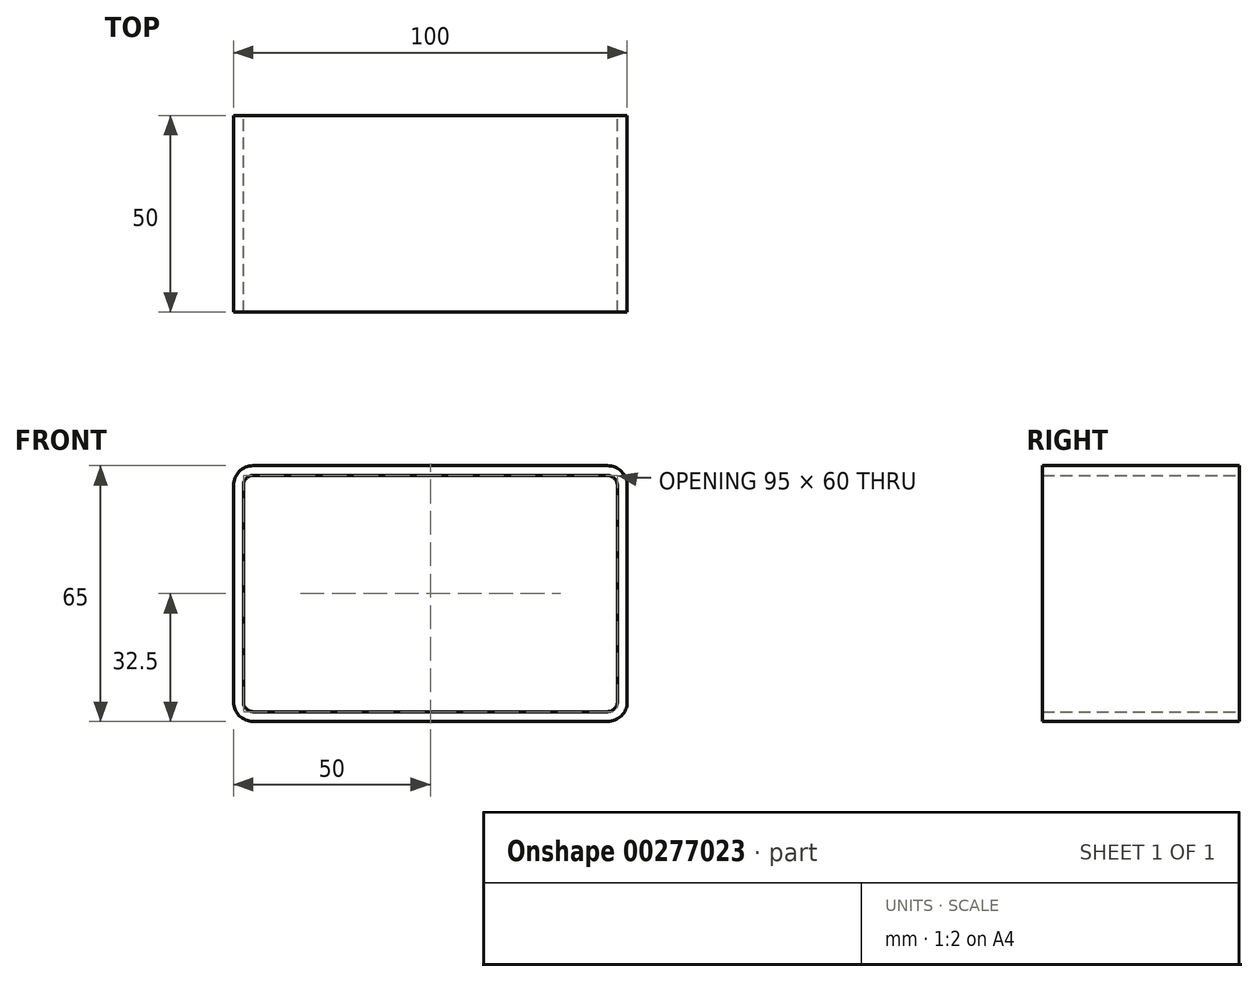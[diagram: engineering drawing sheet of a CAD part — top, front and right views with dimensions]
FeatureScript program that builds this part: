
annotation { "Feature Type Name" : "Feature", "Feature Type Description" : "" }
export const myFeature = defineFeature(function(context is Context, id is Id, definition is map)
    precondition{}
    {
        {
            var Q0;
            Q0=qCreatedBy(makeId("Front.planeOp"),FACE);
            var sketch = newSketch(context, id + "F0", { "sketchPlane" : qUnion([Q0])});
            skLineSegment(sketch, "E0.bottom", {"start": v(50, 32.5) * mm, "end": v(-50, 32.5) * mm});
            skLineSegment(sketch, "E0.top", {"start": v(50, -32.5) * mm, "end": v(-50, -32.5) * mm});
            skLineSegment(sketch, "E0.left", {"start": v(50, 32.5) * mm, "end": v(50, -32.5) * mm});
            skLineSegment(sketch, "E0.right", {"start": v(-50, 32.5) * mm, "end": v(-50, -32.5) * mm});
            skPoint(sketch, "E0.middle", {"position": v(0, 0) * mm});
            skSolve(sketch);
        }
        {
            var Q0;
            Q0 = qSketchRegion(id + "F0", true);
            extrude(context, id + "F1", {"entities" : qUnion([Q0]), "depth" : 50 * mm});
        }
        {
            var Q0;
            Q0=makeQuery(id+"F1.opExtrude","SWEPT_EDGE",EDGE,{"disambiguationData":[OSD([sQuery(id+"F0.wireOp",EDGE,"E0.bottom"),sQuery(id+"F0.wireOp",EDGE,"E0.right")])]});
            var Q1;
            Q1=makeQuery(id+"F1.opExtrude","SWEPT_EDGE",EDGE,{"disambiguationData":[OSD([sQuery(id+"F0.wireOp",EDGE,"E0.top"),sQuery(id+"F0.wireOp",EDGE,"E0.right")])]});
            var Q2;
            Q2=makeQuery(id+"F1.opExtrude","SWEPT_EDGE",EDGE,{"disambiguationData":[OSD([sQuery(id+"F0.wireOp",EDGE,"E0.bottom"),sQuery(id+"F0.wireOp",EDGE,"E0.left")])]});
            var Q3;
            Q3=makeQuery(id+"F1.opExtrude","SWEPT_EDGE",EDGE,{"disambiguationData":[OSD([sQuery(id+"F0.wireOp",EDGE,"E0.top"),sQuery(id+"F0.wireOp",EDGE,"E0.left")])]});
            fillet(context, id + "F2", {"entities" : qUnion([Q0, Q1, Q2, Q3]), "radius" : 5 * mm, "tangentPropagation" : true, "allowEdgeOverflow" : false});
        }
        {
            var Q0;
            Q0=makeQuery(id+"F1.opExtrude","CAP_FACE",FACE,{"disambiguationData":[OSD([sQuery(id+"F0.wireOp",EDGE,"E0.bottom"),sQuery(id+"F0.wireOp",EDGE,"E0.top"),sQuery(id+"F0.wireOp",EDGE,"E0.left"),sQuery(id+"F0.wireOp",EDGE,"E0.right")])],"isStart":false});
            var Q1;
            Q1=makeQuery(id+"F1.opExtrude","CAP_FACE",FACE,{"disambiguationData":[OSD([sQuery(id+"F0.wireOp",EDGE,"E0.bottom"),sQuery(id+"F0.wireOp",EDGE,"E0.top"),sQuery(id+"F0.wireOp",EDGE,"E0.left"),sQuery(id+"F0.wireOp",EDGE,"E0.right")])],"isStart":true});
            shell(context, id + "F3", {"entities" : qUnion([Q0, Q1]), "thickness" : 2.5 * mm});
        }
    });
